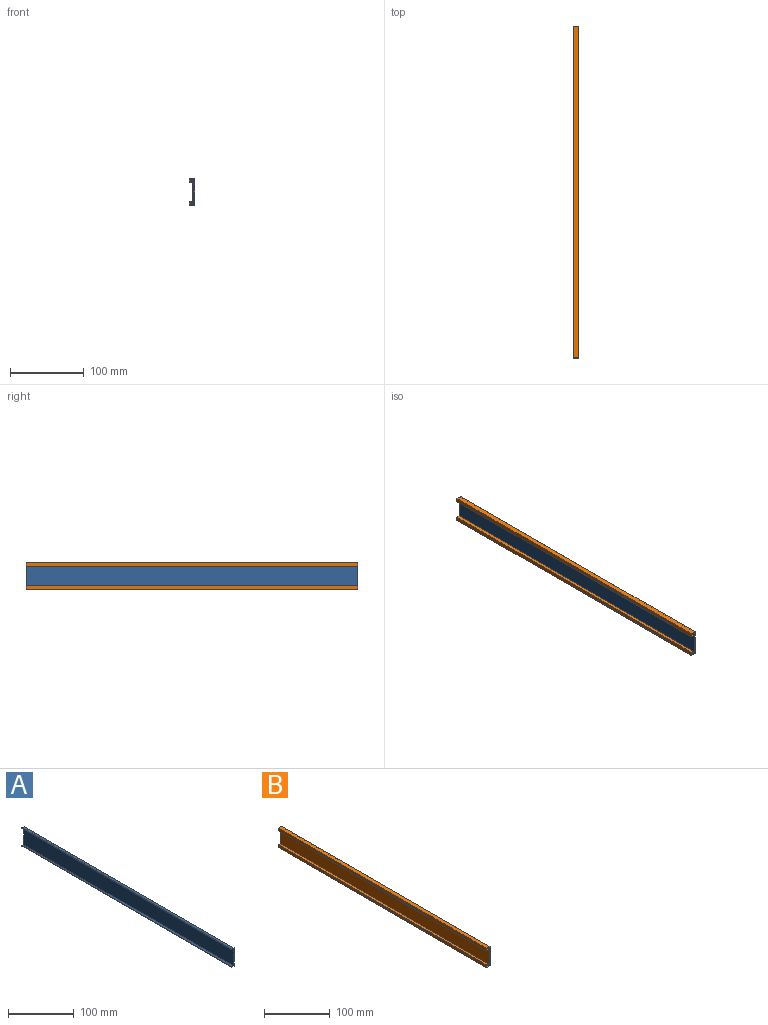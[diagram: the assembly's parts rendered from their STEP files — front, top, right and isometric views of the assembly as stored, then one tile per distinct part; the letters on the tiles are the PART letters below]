
ASSEMBLY  parts=2 mates=1
PART A: 10 faces, bbox 4.5x450x33.5 mm
  f0: plane 450x33.5mm, normal (1,0,0), area 15075mm2, adj f1,f7,f8,f9
  f1: plane 450x4.5mm, normal (0,0,1), area 2025mm2, adj f0,f2,f8,f9
  f2: plane 450x1mm, normal (-1,0,0), area 450mm2, adj f1,f3,f8,f9
  f3: plane 450x3.5mm, normal (0,0,-1), area 1575mm2, adj f2,f4,f8,f9
  f4: plane 450x31.5mm, normal (-1,0,0), area 14175mm2, adj f3,f5,f8,f9
  f5: plane 450x3.5mm, normal (0,0,1), area 1575mm2, adj f4,f6,f8,f9
  f6: plane 450x1mm, normal (-1,0,0), area 450mm2, adj f5,f7,f8,f9
  f7: plane 450x4.5mm, normal (0,0,-1), area 2025mm2, adj f0,f6,f8,f9
  f8: plane 33.5x4.5mm, normal (0,-1,0), area 40.5mm2, adj f0,f1,f2,f3,f4,f5,f6,f7
  f9: plane 33.5x4.5mm, normal (0,1,0), area 40.5mm2, adj f0,f1,f2,f3,f4,f5,f6,f7
PART B: 18 faces, bbox 7x450x36 mm
  f0: plane 450x5mm, normal (0,0,-1), area 2250mm2, adj f1,f15,f16,f17
  f1: plane 450x34mm, normal (-1,0,0), area 15300mm2, adj f0,f2,f16,f17
  f2: plane 450x5mm, normal (0,0,1), area 2250mm2, adj f1,f3,f16,f17
  f3: plane 450x3mm, normal (1,0,0), area 1350mm2, adj f2,f4,f16,f17
  f4: plane 450x3.5mm, normal (0,0,-1), area 1575mm2, adj f3,f5,f16,f17
  f5: plane 450x1mm, normal (1,0,0), area 450mm2, adj f4,f6,f16,f17
  f6: plane 450x4.5mm, normal (0,0,1), area 2025mm2, adj f5,f7,f16,f17
  f7: plane 450x5mm, normal (-1,0,0), area 2250mm2, adj f6,f8,f16,f17
  f8: plane 450x7mm, normal (0,0,-1), area 3150mm2, adj f7,f9,f16,f17
  f9: plane 450x36mm, normal (1,0,0), area 16200mm2, adj f8,f10,f16,f17
  f10: plane 450x7mm, normal (0,0,1), area 3150mm2, adj f9,f11,f16,f17
  f11: plane 450x5mm, normal (-1,0,0), area 2250mm2, adj f10,f12,f16,f17
  f12: plane 450x4.5mm, normal (0,0,-1), area 2023.4mm2, adj f11,f13,f16,f17
  f13: plane 450x1mm, normal (1,0,0), area 450mm2, adj f12,f14,f16,f17
  f14: plane 450x3.5mm, normal (0,0,1), area 1573.4mm2, adj f13,f15,f16,f17
  f15: plane 450x3mm, normal (1,0,0), area 1350mm2, adj f0,f14,f16,f17
  f16: plane 36x7mm, normal (0,-1,0), area 63mm2, adj f0,f1,f2,f3,f4,f5,f6,f7
  f17: plane 36x7mm, normal (0,1,0), area 63mm2, adj f0,f1,f2,f3,f4,f5,f6,f7
PLACE A t=(-115.43,122.74,-46.05)mm
PLACE B t=(-115.43,122.74,-46.05)mm fixed
MATE slider B.f16 <-> A.f8  axis (0,-1,0) through (-129.56,-327.26,-27.82)mm
